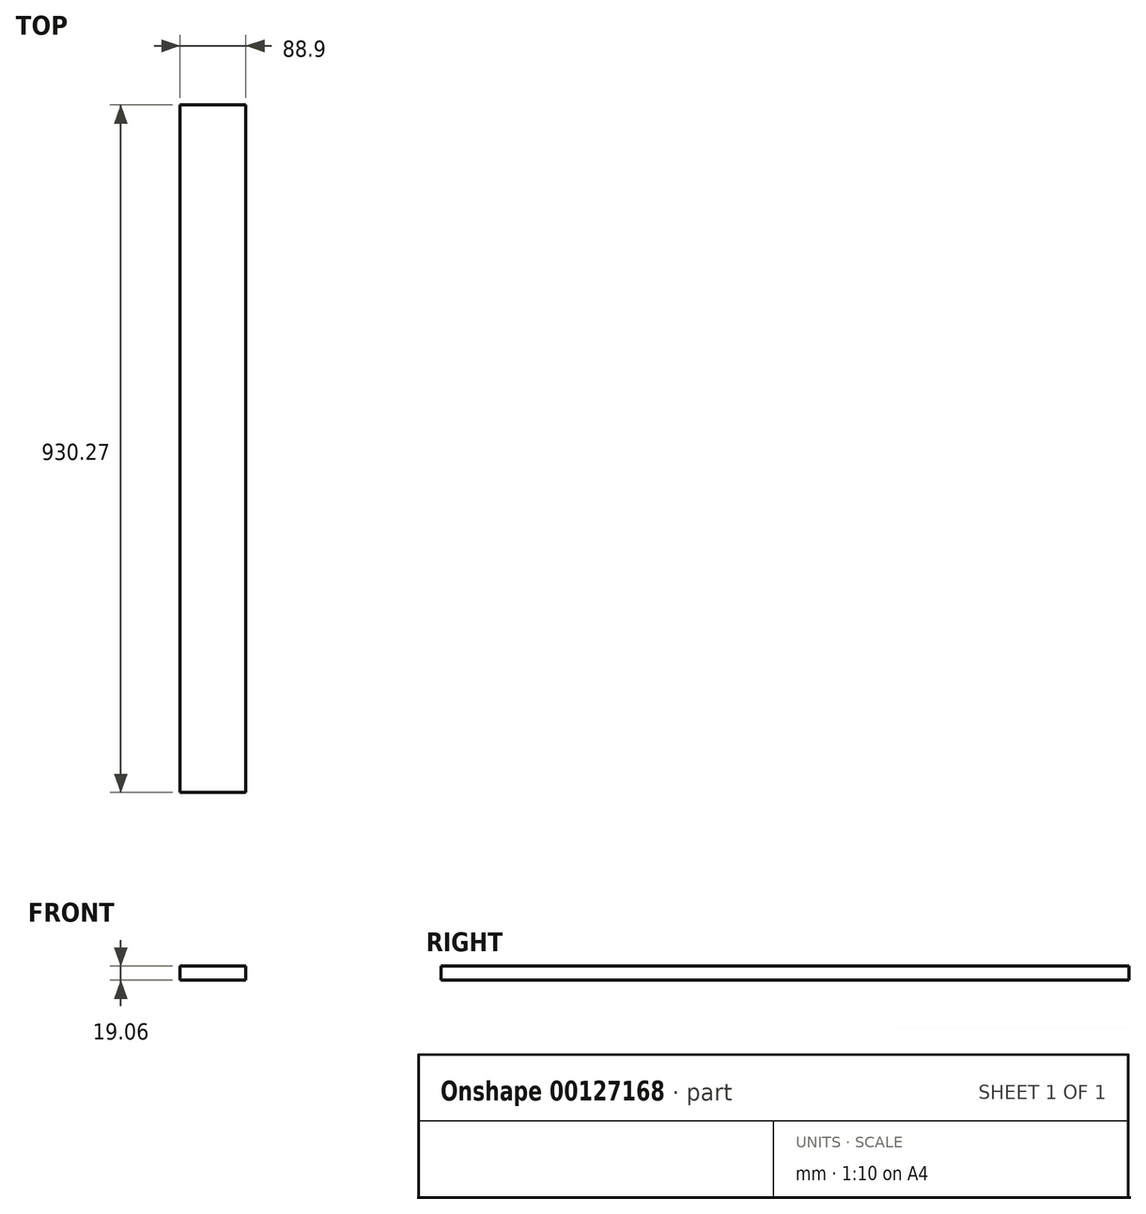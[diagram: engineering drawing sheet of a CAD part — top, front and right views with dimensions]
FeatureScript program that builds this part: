
annotation { "Feature Type Name" : "Feature", "Feature Type Description" : "" }
export const myFeature = defineFeature(function(context is Context, id is Id, definition is map)
    precondition{}
    {
        {
            var Q0;
            Q0=qCreatedBy(makeId("Front.planeOp"),FACE);
            var sketch = newSketch(context, id + "F0", { "sketchPlane" : qUnion([Q0])});
            skLineSegment(sketch, "E0.bottom", {"start": v(44.45, -9.52) * mm, "end": v(-44.45, -9.53) * mm});
            skLineSegment(sketch, "E0.top", {"start": v(44.45, 9.53) * mm, "end": v(-44.45, 9.53) * mm});
            skLineSegment(sketch, "E0.left", {"start": v(44.45, -9.52) * mm, "end": v(44.45, 9.53) * mm});
            skLineSegment(sketch, "E0.right", {"start": v(-44.45, -9.53) * mm, "end": v(-44.45, 9.53) * mm});
            skPoint(sketch, "E0.middle", {"position": v(0, 0) * mm});
            skSolve(sketch);
        }
        {
            var Q0;
            Q0=qSketchRegion(id+"F0",true);
            extrude(context, id + "F1", {"entities" : qUnion([Q0]), "depth" : 930.27 * mm});
        }
    });
